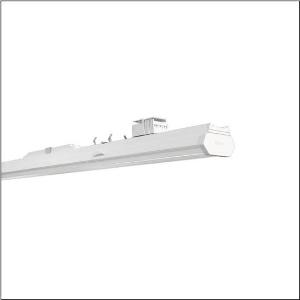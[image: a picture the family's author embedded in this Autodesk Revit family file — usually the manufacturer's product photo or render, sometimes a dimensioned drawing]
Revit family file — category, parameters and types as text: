
# Revit family: licross_r__11_protected_mo_51tp11cn58xf_4d9e
name_source: partatom
category: Lighting Fixtures
units: mm (PartAtom-declared; Revit-internal decimal feet)

## family parameters
Cut with Voids When Loaded = No
Host = Face
Light Source = No
Part Type = Normal
Room Calculation Point = No
Round Connector Dimension = Use Diameter
Shared = No

## types (1)
- --- (1 x LED, 8150 lm, 49 W, 5000K)
    Apparent Load = 49 VA
    CIE Flux Codes = 83 94 98 100 100
    Color Rendering = 80
    Color Temperature = 5000K
    Default Elevation = 1800 mm
    Description = Licross® 11 Protected MO, luminaire insert, of sheet steel, galvanised, coil coated, white, length: 1.500mm, width: 90mm, height: 101mm, LED rated luminous flux: 8.150lm, light colour: 850, control gear: ON/OFF Multilumen, CLOi, control gear: ECG Multilumen, with plug, 3-pole, with phase selection, mains connection: 220..240V, AC, 50/60Hz, start of lifetime: 49W, end of service life: 54W, halogen-free wiring, primary optical cover: cover, of PMMA, light emission: direct distribution, primary light characteristic: symmetric, protection rating (complete): IP64, insulation class (complete): insulation class I (protective earthing), certification: CE, ENEC, VDE, UKCA, protection symbol: D if used in an environment with conductive dust loads with corresponding accessories, impact resistance: IK06, permissible ambient temperature for indoor applications: -35..+40°C, corresponds to IFS (International Featured Standards) requirements for safety and quality in the food industry, reducing of maximum allowable ambient temperature of 5°C with ceiling mounting, LABS conformity tested according to VDMA 24364:2018-05, packaging unit: 1 piece
    Height = 92 mm
    Lamp = 1 x LED
    Lamp Light Flux = 8150 lm
    Lamp Power = 49 W
    Lamp count = 1
    Length = 1500 mm
    Luminous efficacy = 166 lm/W
    Manufacturer = Siteco
    ModVariant = No
    Model = 51TP11CN58XF
    Mounting Place = Ceiling
    Mounting Type = Pendant
    Number of Poles = 1
    OnlyDefault = Yes
    Power Factor = 1
    Product Name = Licross® 11 Protected MO
    Product group = luminaire insert
    ProductGroupID = 901
    Protection Class = Protection class I
    Protection Degree = IP 64
    RLX_Detail_Level = 1
    RLX_Emergency_Light_Flux = 0 lm
    RLX_Emergency_Type = 0
    RLX_Emergency_Type_DB = No
    RlxData = <blob elided: 21825 chars, md5=795e1f3e>
    Socket = socket
    Standby Power = 0 W
    System Light Flux = 8150 lm
    System Power = 49 W
    Type Comments = factory setting: luminous flux: 100 % | (A | C | E) | 111 mA
    Type Image = l_1256148.jpg
    URL = http://relux.com
    VarID = @adj_158327
    Voltage = 0 V
    Weight = 0.00 kg
    Width = 88 mm

## geometry (parser evidence)
native form markers: Blend x4, Sweep x11
no freeform markers — native parametric forms only
